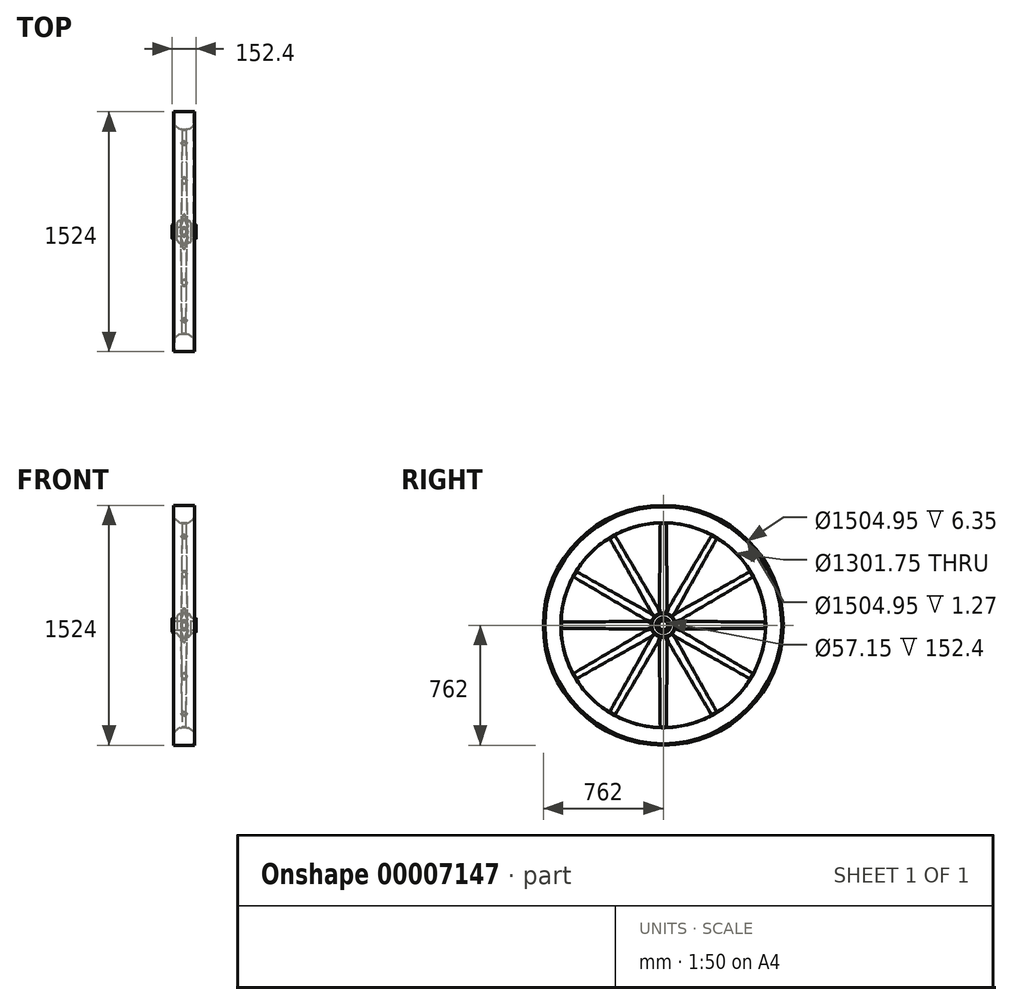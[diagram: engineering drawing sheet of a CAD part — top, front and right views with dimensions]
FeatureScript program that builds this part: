
annotation { "Feature Type Name" : "Feature", "Feature Type Description" : "" }
export const myFeature = defineFeature(function(context is Context, id is Id, definition is map)
    precondition{}
    {
        {
            var Q0;
            Q0=qCreatedBy(makeId("Front.planeOp"),FACE);
            var sketch = newSketch(context, id + "F0", { "sketchPlane" : qUnion([Q0])});
            skLineSegment(sketch, "E0", {"start": v(-76.2, 28.57) * mm, "end": v(76.2, 28.57) * mm});
            skLineSegment(sketch, "E1", {"start": v(76.2, 28.57) * mm, "end": v(76.2, 47.62) * mm});
            skLineSegment(sketch, "E2", {"start": v(76.2, 47.62) * mm, "end": v(44.45, 47.62) * mm});
            skLineSegment(sketch, "E3", {"start": v(44.45, 47.62) * mm, "end": v(44.45, 55.24) * mm});
            skLineSegment(sketch, "E4", {"start": v(44.45, 55.24) * mm, "end": v(31.75, 73.02) * mm});
            skLineSegment(sketch, "E5", {"start": v(31.75, 73.03) * mm, "end": v(-31.75, 73.03) * mm});
            skLineSegment(sketch, "E6", {"start": v(-31.75, 73.02) * mm, "end": v(-44.45, 55.24) * mm});
            skLineSegment(sketch, "E7", {"start": v(-44.45, 55.24) * mm, "end": v(-44.45, 47.62) * mm});
            skLineSegment(sketch, "E8", {"start": v(-44.45, 47.62) * mm, "end": v(-76.2, 47.62) * mm});
            skLineSegment(sketch, "E9", {"start": v(-76.2, 47.62) * mm, "end": v(-76.2, 28.58) * mm});
            skLineSegment(sketch, "E10", {"start": v(109.3, 0) * mm, "end": v(-114.89, 0) * mm, "construction": true});
            skLineSegment(sketch, "E11", {"start": v(-66.68, 762) * mm, "end": v(66.67, 762) * mm});
            skLineSegment(sketch, "E12", {"start": v(66.67, 762) * mm, "end": v(66.67, 752.48) * mm});
            skLineSegment(sketch, "E13", {"start": v(66.67, 752.48) * mm, "end": v(60.32, 752.48) * mm});
            skLineSegment(sketch, "E14", {"start": v(60.32, 752.48) * mm, "end": v(60.32, 676.28) * mm});
            skLineSegment(sketch, "E15", {"start": v(60.32, 676.28) * mm, "end": v(28.57, 650.88) * mm});
            skLineSegment(sketch, "E16", {"start": v(28.57, 650.88) * mm, "end": v(-28.58, 650.88) * mm});
            skLineSegment(sketch, "E17", {"start": v(-28.58, 650.88) * mm, "end": v(-60.33, 676.28) * mm});
            skLineSegment(sketch, "E18", {"start": v(-60.33, 676.28) * mm, "end": v(-60.33, 752.48) * mm});
            skLineSegment(sketch, "E19", {"start": v(-60.33, 752.48) * mm, "end": v(-66.68, 752.48) * mm});
            skLineSegment(sketch, "E20", {"start": v(-66.68, 752.48) * mm, "end": v(-66.68, 762) * mm});
            skSolve(sketch);
        }
        {
            var Q0;
            Q0=makeQuery(id+"F0.imprint","IMPRINT",FACE,{"disambiguationData":[TD([[makeQuery(id+"F0.imprint","IMPRINT",EDGE,{"derivedFrom":sQuery(id+"F0.wireOp",EDGE,"E11")}),-1.0]])]});
            var Q1;
            Q1=makeQuery(id+"F0.imprint","IMPRINT",FACE,{"disambiguationData":[TD([[makeQuery(id+"F0.imprint","IMPRINT",EDGE,{"derivedFrom":sQuery(id+"F0.wireOp",EDGE,"E0")}),1.0]])]});
            var Q2;
            Q2=sQuery(id+"F0.wireOp",EDGE,"E10");
            revolve(context, id + "F1", {"entities" : qUnion([Q0, Q1]), "axis" : qUnion([Q2]), "revolveType" : RevolveType.FULL});
        }
        {
            var Q0;
            Q0=makeQuery(id+"F1.opRevolve","SWEPT_EDGE",EDGE,{"disambiguationData":[OSD([sQuery(id+"F0.wireOp",EDGE,"E7"),sQuery(id+"F0.wireOp",EDGE,"E8")])]});
            var Q1;
            Q1=makeQuery(id+"F1.opRevolve","SWEPT_EDGE",EDGE,{"disambiguationData":[OSD([sQuery(id+"F0.wireOp",EDGE,"E6"),sQuery(id+"F0.wireOp",EDGE,"E7")])]});
            var Q2;
            Q2=makeQuery(id+"F1.opRevolve","SWEPT_EDGE",EDGE,{"disambiguationData":[OSD([sQuery(id+"F0.wireOp",EDGE,"E5"),sQuery(id+"F0.wireOp",EDGE,"E6")])]});
            var Q3;
            Q3=makeQuery(id+"F1.opRevolve","SWEPT_EDGE",EDGE,{"disambiguationData":[OSD([sQuery(id+"F0.wireOp",EDGE,"E4"),sQuery(id+"F0.wireOp",EDGE,"E5")])]});
            var Q4;
            Q4=makeQuery(id+"F1.opRevolve","SWEPT_EDGE",EDGE,{"disambiguationData":[OSD([sQuery(id+"F0.wireOp",EDGE,"E3"),sQuery(id+"F0.wireOp",EDGE,"E4")])]});
            var Q5;
            Q5=makeQuery(id+"F1.opRevolve","SWEPT_EDGE",EDGE,{"disambiguationData":[OSD([sQuery(id+"F0.wireOp",EDGE,"E2"),sQuery(id+"F0.wireOp",EDGE,"E3")])]});
            fillet(context, id + "F2", {"entities" : qUnion([Q0, Q1, Q2, Q3, Q4, Q5]), "radius" : 5.08 * mm, "tangentPropagation" : true, "allowEdgeOverflow" : false});
        }
        {
            var Q0;
            Q0=makeQuery(id+"F1.opRevolve","SWEPT_EDGE",EDGE,{"disambiguationData":[OSD([sQuery(id+"F0.wireOp",EDGE,"E1"),sQuery(id+"F0.wireOp",EDGE,"E2")])]});
            var Q1;
            Q1=makeQuery(id+"F1.opRevolve","SWEPT_EDGE",EDGE,{"disambiguationData":[OSD([sQuery(id+"F0.wireOp",EDGE,"E8"),sQuery(id+"F0.wireOp",EDGE,"E9")])]});
            fillet(context, id + "F3", {"entities" : qUnion([Q0, Q1]), "radius" : 7.62 * mm, "tangentPropagation" : true, "allowEdgeOverflow" : false});
        }
        {
            var Q0;
            Q0=makeQuery(id+"F1.opRevolve","SWEPT_EDGE",EDGE,{"disambiguationData":[OSD([sQuery(id+"F0.wireOp",EDGE,"E17"),sQuery(id+"F0.wireOp",EDGE,"E18")])]});
            var Q1;
            Q1=makeQuery(id+"F1.opRevolve","SWEPT_EDGE",EDGE,{"disambiguationData":[OSD([sQuery(id+"F0.wireOp",EDGE,"E16"),sQuery(id+"F0.wireOp",EDGE,"E17")])]});
            var Q2;
            Q2=makeQuery(id+"F1.opRevolve","SWEPT_EDGE",EDGE,{"disambiguationData":[OSD([sQuery(id+"F0.wireOp",EDGE,"E15"),sQuery(id+"F0.wireOp",EDGE,"E16")])]});
            var Q3;
            Q3=makeQuery(id+"F1.opRevolve","SWEPT_EDGE",EDGE,{"disambiguationData":[OSD([sQuery(id+"F0.wireOp",EDGE,"E14"),sQuery(id+"F0.wireOp",EDGE,"E15")])]});
            fillet(context, id + "F4", {"entities" : qUnion([Q0, Q1, Q2, Q3]), "radius" : 12.7 * mm, "tangentPropagation" : true, "allowEdgeOverflow" : false});
        }
        {
            var Q0;
            Q0=makeQuery(id+"F1.opRevolve","SWEPT_EDGE",EDGE,{"disambiguationData":[OSD([sQuery(id+"F0.wireOp",EDGE,"E13"),sQuery(id+"F0.wireOp",EDGE,"E14")])]});
            fillet(context, id + "F5", {"entities" : qUnion([Q0]), "radius" : 5.08 * mm, "tangentPropagation" : true, "allowEdgeOverflow" : false});
        }
        {
            var Q0;
            Q0=qCreatedBy(makeId("Front.planeOp"),FACE);
            cPlane(context, id + "F6", {"entities" : qUnion([Q0]), "cplaneType" : CPlaneType.OFFSET, "offset" : 50.8 * mm, "oppositeDirection" : true, "width" : 152.4 * mm, "height" : 152.4 * mm});
        }
        {
            var Q0;
            Q0=qCreatedBy(makeId("Front.planeOp"),FACE);
            cPlane(context, id + "F7", {"entities" : qUnion([Q0]), "cplaneType" : CPlaneType.OFFSET, "offset" : 654.05 * mm, "oppositeDirection" : true, "width" : 152.4 * mm, "height" : 152.4 * mm});
        }
        {
            var Q0;
            Q0=qCreatedBy(id+"F6.planeOp",FACE);
            var sketch = newSketch(context, id + "F8", { "sketchPlane" : qUnion([Q0])});
            skEllipse(sketch, "E21", {"center": v(0, 0) * mm, "majorRadius": 25.4 * mm, "minorRadius": 19.05 * mm, "majorAxis": v(0, 1)});
            skSolve(sketch);
        }
        {
            var Q0;
            Q0=qCreatedBy(id+"F7.planeOp",FACE);
            var sketch = newSketch(context, id + "F9", { "sketchPlane" : qUnion([Q0])});
            skEllipse(sketch, "E22", {"center": v(0, 0) * mm, "majorRadius": 19.05 * mm, "minorRadius": 12.7 * mm, "majorAxis": v(0, 1)});
            skSolve(sketch);
        }
        {
            var Q0;
            Q0=makeQuery(id+"F8.imprint","IMPRINT",FACE,{"disambiguationData":[TD([[makeQuery(id+"F8.imprint","IMPRINT",EDGE,{"derivedFrom":sQuery(id+"F8.wireOp",EDGE,"E21")}),1.0]])]});
            var Q1;
            Q1=makeQuery(id+"F9.imprint","IMPRINT",FACE,{"disambiguationData":[TD([[makeQuery(id+"F9.imprint","IMPRINT",EDGE,{"derivedFrom":sQuery(id+"F9.wireOp",EDGE,"E22")}),1.0]])]});
            loft(context, id + "F10", {"sheetProfilesArray" : [{ "sheetProfileEntities" : qUnion([Q0]) }, { "sheetProfileEntities" : qUnion([Q1]) }]});
        }
        {
            var Q0;
            Q0=makeQuery(id+"F10.opLoft","SWEPT_BODY",BODY,{"disambiguationData":[OSD([makeQuery(id+"F8.imprint","IMPRINT",FACE,{"disambiguationData":[TD([[makeQuery(id+"F8.imprint","IMPRINT",EDGE,{"derivedFrom":sQuery(id+"F8.wireOp",EDGE,"E21")}),1.0]])]}),makeQuery(id+"F9.imprint","IMPRINT",FACE,{"disambiguationData":[TD([[makeQuery(id+"F9.imprint","IMPRINT",EDGE,{"derivedFrom":sQuery(id+"F9.wireOp",EDGE,"E22")}),1.0]])]})])]});
            var Q1;
            Q1=makeQuery(id+"F1.opRevolve","SWEPT_EDGE",EDGE,{"disambiguationData":[OSD([sQuery(id+"F0.wireOp",EDGE,"E0"),sQuery(id+"F0.wireOp",EDGE,"E1")])]});
            circularPattern(context, id + "F11", {"entities" : qUnion([Q0]), "axis" : qUnion([Q1]), "angle" : 30 * degree, "instanceCount" : 12});
        }
        {
            var Q0;
            Q0=makeQuery(id+"F10.opLoft","SWEPT_BODY",BODY,{"disambiguationData":[OSD([makeQuery(id+"F8.imprint","IMPRINT",FACE,{"disambiguationData":[TD([[makeQuery(id+"F8.imprint","IMPRINT",EDGE,{"derivedFrom":sQuery(id+"F8.wireOp",EDGE,"E21")}),1.0]])]}),makeQuery(id+"F9.imprint","IMPRINT",FACE,{"disambiguationData":[TD([[makeQuery(id+"F9.imprint","IMPRINT",EDGE,{"derivedFrom":sQuery(id+"F9.wireOp",EDGE,"E22")}),1.0]])]})])]});
            var Q1;
            Q1=makeQuery(id+"F1.opRevolve","SWEPT_BODY",BODY,{"disambiguationData":[OSD([sQuery(id+"F0.wireOp",EDGE,"E0"),sQuery(id+"F0.wireOp",EDGE,"E1"),sQuery(id+"F0.wireOp",EDGE,"E2"),sQuery(id+"F0.wireOp",EDGE,"E3"),sQuery(id+"F0.wireOp",EDGE,"E4"),sQuery(id+"F0.wireOp",EDGE,"E5"),sQuery(id+"F0.wireOp",EDGE,"E6"),sQuery(id+"F0.wireOp",EDGE,"E7"),sQuery(id+"F0.wireOp",EDGE,"E8"),sQuery(id+"F0.wireOp",EDGE,"E9")])]});
            var Q2;
            Q2=makeQuery(id+"F11.opPattern","COPY",BODY,{"derivedFrom":makeQuery(id+"F10.opLoft","SWEPT_BODY",BODY,{"disambiguationData":[OSD([makeQuery(id+"F8.imprint","IMPRINT",FACE,{"disambiguationData":[TD([[makeQuery(id+"F8.imprint","IMPRINT",EDGE,{"derivedFrom":sQuery(id+"F8.wireOp",EDGE,"E21")}),1.0]])]}),makeQuery(id+"F9.imprint","IMPRINT",FACE,{"disambiguationData":[TD([[makeQuery(id+"F9.imprint","IMPRINT",EDGE,{"derivedFrom":sQuery(id+"F9.wireOp",EDGE,"E22")}),1.0]])]})])]}),"instanceName":"1"});
            var Q3;
            Q3=makeQuery(id+"F11.opPattern","COPY",BODY,{"derivedFrom":makeQuery(id+"F10.opLoft","SWEPT_BODY",BODY,{"disambiguationData":[OSD([makeQuery(id+"F8.imprint","IMPRINT",FACE,{"disambiguationData":[TD([[makeQuery(id+"F8.imprint","IMPRINT",EDGE,{"derivedFrom":sQuery(id+"F8.wireOp",EDGE,"E21")}),1.0]])]}),makeQuery(id+"F9.imprint","IMPRINT",FACE,{"disambiguationData":[TD([[makeQuery(id+"F9.imprint","IMPRINT",EDGE,{"derivedFrom":sQuery(id+"F9.wireOp",EDGE,"E22")}),1.0]])]})])]}),"instanceName":"2"});
            var Q4;
            Q4=makeQuery(id+"F11.opPattern","COPY",BODY,{"derivedFrom":makeQuery(id+"F10.opLoft","SWEPT_BODY",BODY,{"disambiguationData":[OSD([makeQuery(id+"F8.imprint","IMPRINT",FACE,{"disambiguationData":[TD([[makeQuery(id+"F8.imprint","IMPRINT",EDGE,{"derivedFrom":sQuery(id+"F8.wireOp",EDGE,"E21")}),1.0]])]}),makeQuery(id+"F9.imprint","IMPRINT",FACE,{"disambiguationData":[TD([[makeQuery(id+"F9.imprint","IMPRINT",EDGE,{"derivedFrom":sQuery(id+"F9.wireOp",EDGE,"E22")}),1.0]])]})])]}),"instanceName":"3"});
            var Q5;
            Q5=makeQuery(id+"F11.opPattern","COPY",BODY,{"derivedFrom":makeQuery(id+"F10.opLoft","SWEPT_BODY",BODY,{"disambiguationData":[OSD([makeQuery(id+"F8.imprint","IMPRINT",FACE,{"disambiguationData":[TD([[makeQuery(id+"F8.imprint","IMPRINT",EDGE,{"derivedFrom":sQuery(id+"F8.wireOp",EDGE,"E21")}),1.0]])]}),makeQuery(id+"F9.imprint","IMPRINT",FACE,{"disambiguationData":[TD([[makeQuery(id+"F9.imprint","IMPRINT",EDGE,{"derivedFrom":sQuery(id+"F9.wireOp",EDGE,"E22")}),1.0]])]})])]}),"instanceName":"4"});
            var Q6;
            Q6=makeQuery(id+"F11.opPattern","COPY",BODY,{"derivedFrom":makeQuery(id+"F10.opLoft","SWEPT_BODY",BODY,{"disambiguationData":[OSD([makeQuery(id+"F8.imprint","IMPRINT",FACE,{"disambiguationData":[TD([[makeQuery(id+"F8.imprint","IMPRINT",EDGE,{"derivedFrom":sQuery(id+"F8.wireOp",EDGE,"E21")}),1.0]])]}),makeQuery(id+"F9.imprint","IMPRINT",FACE,{"disambiguationData":[TD([[makeQuery(id+"F9.imprint","IMPRINT",EDGE,{"derivedFrom":sQuery(id+"F9.wireOp",EDGE,"E22")}),1.0]])]})])]}),"instanceName":"5"});
            var Q7;
            Q7=makeQuery(id+"F11.opPattern","COPY",BODY,{"derivedFrom":makeQuery(id+"F10.opLoft","SWEPT_BODY",BODY,{"disambiguationData":[OSD([makeQuery(id+"F8.imprint","IMPRINT",FACE,{"disambiguationData":[TD([[makeQuery(id+"F8.imprint","IMPRINT",EDGE,{"derivedFrom":sQuery(id+"F8.wireOp",EDGE,"E21")}),1.0]])]}),makeQuery(id+"F9.imprint","IMPRINT",FACE,{"disambiguationData":[TD([[makeQuery(id+"F9.imprint","IMPRINT",EDGE,{"derivedFrom":sQuery(id+"F9.wireOp",EDGE,"E22")}),1.0]])]})])]}),"instanceName":"6"});
            var Q8;
            Q8=makeQuery(id+"F11.opPattern","COPY",BODY,{"derivedFrom":makeQuery(id+"F10.opLoft","SWEPT_BODY",BODY,{"disambiguationData":[OSD([makeQuery(id+"F8.imprint","IMPRINT",FACE,{"disambiguationData":[TD([[makeQuery(id+"F8.imprint","IMPRINT",EDGE,{"derivedFrom":sQuery(id+"F8.wireOp",EDGE,"E21")}),1.0]])]}),makeQuery(id+"F9.imprint","IMPRINT",FACE,{"disambiguationData":[TD([[makeQuery(id+"F9.imprint","IMPRINT",EDGE,{"derivedFrom":sQuery(id+"F9.wireOp",EDGE,"E22")}),1.0]])]})])]}),"instanceName":"7"});
            var Q9;
            Q9=makeQuery(id+"F11.opPattern","COPY",BODY,{"derivedFrom":makeQuery(id+"F10.opLoft","SWEPT_BODY",BODY,{"disambiguationData":[OSD([makeQuery(id+"F8.imprint","IMPRINT",FACE,{"disambiguationData":[TD([[makeQuery(id+"F8.imprint","IMPRINT",EDGE,{"derivedFrom":sQuery(id+"F8.wireOp",EDGE,"E21")}),1.0]])]}),makeQuery(id+"F9.imprint","IMPRINT",FACE,{"disambiguationData":[TD([[makeQuery(id+"F9.imprint","IMPRINT",EDGE,{"derivedFrom":sQuery(id+"F9.wireOp",EDGE,"E22")}),1.0]])]})])]}),"instanceName":"8"});
            var Q10;
            Q10=makeQuery(id+"F11.opPattern","COPY",BODY,{"derivedFrom":makeQuery(id+"F10.opLoft","SWEPT_BODY",BODY,{"disambiguationData":[OSD([makeQuery(id+"F8.imprint","IMPRINT",FACE,{"disambiguationData":[TD([[makeQuery(id+"F8.imprint","IMPRINT",EDGE,{"derivedFrom":sQuery(id+"F8.wireOp",EDGE,"E21")}),1.0]])]}),makeQuery(id+"F9.imprint","IMPRINT",FACE,{"disambiguationData":[TD([[makeQuery(id+"F9.imprint","IMPRINT",EDGE,{"derivedFrom":sQuery(id+"F9.wireOp",EDGE,"E22")}),1.0]])]})])]}),"instanceName":"9"});
            var Q11;
            Q11=makeQuery(id+"F11.opPattern","COPY",BODY,{"derivedFrom":makeQuery(id+"F10.opLoft","SWEPT_BODY",BODY,{"disambiguationData":[OSD([makeQuery(id+"F8.imprint","IMPRINT",FACE,{"disambiguationData":[TD([[makeQuery(id+"F8.imprint","IMPRINT",EDGE,{"derivedFrom":sQuery(id+"F8.wireOp",EDGE,"E21")}),1.0]])]}),makeQuery(id+"F9.imprint","IMPRINT",FACE,{"disambiguationData":[TD([[makeQuery(id+"F9.imprint","IMPRINT",EDGE,{"derivedFrom":sQuery(id+"F9.wireOp",EDGE,"E22")}),1.0]])]})])]}),"instanceName":"10"});
            var Q12;
            Q12=makeQuery(id+"F11.opPattern","COPY",BODY,{"derivedFrom":makeQuery(id+"F10.opLoft","SWEPT_BODY",BODY,{"disambiguationData":[OSD([makeQuery(id+"F8.imprint","IMPRINT",FACE,{"disambiguationData":[TD([[makeQuery(id+"F8.imprint","IMPRINT",EDGE,{"derivedFrom":sQuery(id+"F8.wireOp",EDGE,"E21")}),1.0]])]}),makeQuery(id+"F9.imprint","IMPRINT",FACE,{"disambiguationData":[TD([[makeQuery(id+"F9.imprint","IMPRINT",EDGE,{"derivedFrom":sQuery(id+"F9.wireOp",EDGE,"E22")}),1.0]])]})])]}),"instanceName":"11"});
            booleanBodies(context, id + "F12", {"operationType" : BooleanOperationType.UNION, "tools" : qUnion([Q0, Q1, Q2, Q3, Q4, Q5, Q6, Q7, Q8, Q9, Q10, Q11, Q12])});
        }
        {
            var Q0;
            {var subQ0=makeQuery(id+"F10.opLoft","SWEPT_FACE",FACE,{"disambiguationData":[OSD([sQuery(id+"F8.wireOp",EDGE,"E21"),sQuery(id+"F9.wireOp",EDGE,"E22")])]});Q0=makeQuery(id+"F12.opBoolean","INTERSECT",EDGE,{"derivedFrom":[subQ0,makeQuery(id+"F11.opPattern","COPY",FACE,{"derivedFrom":subQ0,"instanceName":"11"})]});}
            var Q1;
            Q1=makeQuery(id+"F12.opBoolean","INTERSECT",EDGE,{"disambiguationData":[OD(0.0)],"derivedFrom":[makeQuery(id+"F1.opRevolve","SWEPT_FACE",FACE,{"disambiguationData":[OSD([sQuery(id+"F0.wireOp",EDGE,"E5")])]}),makeQuery(id+"F10.opLoft","SWEPT_FACE",FACE,{"disambiguationData":[OSD([sQuery(id+"F8.wireOp",EDGE,"E21"),sQuery(id+"F9.wireOp",EDGE,"E22")])]})]});
            var Q2;
            Q2=makeQuery(id+"F12.opBoolean","INTERSECT",EDGE,{"disambiguationData":[OD(0.0)],"derivedFrom":[makeQuery(id+"F1.opRevolve","SWEPT_FACE",FACE,{"disambiguationData":[OSD([sQuery(id+"F0.wireOp",EDGE,"E5")])]}),makeQuery(id+"F11.opPattern","COPY",FACE,{"derivedFrom":makeQuery(id+"F10.opLoft","SWEPT_FACE",FACE,{"disambiguationData":[OSD([sQuery(id+"F8.wireOp",EDGE,"E21"),sQuery(id+"F9.wireOp",EDGE,"E22")])]}),"instanceName":"11"})]});
            var Q3;
            Q3=makeQuery(id+"F12.opBoolean","INTERSECT",EDGE,{"disambiguationData":[OD(0.0)],"derivedFrom":[makeQuery(id+"F1.opRevolve","SWEPT_FACE",FACE,{"disambiguationData":[OSD([sQuery(id+"F0.wireOp",EDGE,"E5")])]}),makeQuery(id+"F11.opPattern","COPY",FACE,{"derivedFrom":makeQuery(id+"F10.opLoft","SWEPT_FACE",FACE,{"disambiguationData":[OSD([sQuery(id+"F8.wireOp",EDGE,"E21"),sQuery(id+"F9.wireOp",EDGE,"E22")])]}),"instanceName":"10"})]});
            var Q4;
            {var subQ0=makeQuery(id+"F10.opLoft","SWEPT_FACE",FACE,{"disambiguationData":[OSD([sQuery(id+"F8.wireOp",EDGE,"E21"),sQuery(id+"F9.wireOp",EDGE,"E22")])]});Q4=makeQuery(id+"F12.opBoolean","INTERSECT",EDGE,{"derivedFrom":[makeQuery(id+"F11.opPattern","COPY",FACE,{"derivedFrom":subQ0,"instanceName":"10"}),makeQuery(id+"F11.opPattern","COPY",FACE,{"derivedFrom":subQ0,"instanceName":"11"})]});}
            var Q5;
            {var subQ0=makeQuery(id+"F10.opLoft","SWEPT_FACE",FACE,{"disambiguationData":[OSD([sQuery(id+"F8.wireOp",EDGE,"E21"),sQuery(id+"F9.wireOp",EDGE,"E22")])]});Q5=makeQuery(id+"F12.opBoolean","INTERSECT",EDGE,{"derivedFrom":[makeQuery(id+"F11.opPattern","COPY",FACE,{"derivedFrom":subQ0,"instanceName":"9"}),makeQuery(id+"F11.opPattern","COPY",FACE,{"derivedFrom":subQ0,"instanceName":"10"})]});}
            var Q6;
            Q6=makeQuery(id+"F12.opBoolean","INTERSECT",EDGE,{"disambiguationData":[OD(0.0)],"derivedFrom":[makeQuery(id+"F1.opRevolve","SWEPT_FACE",FACE,{"disambiguationData":[OSD([sQuery(id+"F0.wireOp",EDGE,"E5")])]}),makeQuery(id+"F11.opPattern","COPY",FACE,{"derivedFrom":makeQuery(id+"F10.opLoft","SWEPT_FACE",FACE,{"disambiguationData":[OSD([sQuery(id+"F8.wireOp",EDGE,"E21"),sQuery(id+"F9.wireOp",EDGE,"E22")])]}),"instanceName":"9"})]});
            var Q7;
            {var subQ0=makeQuery(id+"F10.opLoft","SWEPT_FACE",FACE,{"disambiguationData":[OSD([sQuery(id+"F8.wireOp",EDGE,"E21"),sQuery(id+"F9.wireOp",EDGE,"E22")])]});Q7=makeQuery(id+"F12.opBoolean","INTERSECT",EDGE,{"derivedFrom":[makeQuery(id+"F11.opPattern","COPY",FACE,{"derivedFrom":subQ0,"instanceName":"8"}),makeQuery(id+"F11.opPattern","COPY",FACE,{"derivedFrom":subQ0,"instanceName":"9"})]});}
            var Q8;
            Q8=makeQuery(id+"F12.opBoolean","INTERSECT",EDGE,{"disambiguationData":[OD(0.0)],"derivedFrom":[makeQuery(id+"F1.opRevolve","SWEPT_FACE",FACE,{"disambiguationData":[OSD([sQuery(id+"F0.wireOp",EDGE,"E5")])]}),makeQuery(id+"F11.opPattern","COPY",FACE,{"derivedFrom":makeQuery(id+"F10.opLoft","SWEPT_FACE",FACE,{"disambiguationData":[OSD([sQuery(id+"F8.wireOp",EDGE,"E21"),sQuery(id+"F9.wireOp",EDGE,"E22")])]}),"instanceName":"8"})]});
            var Q9;
            {var subQ0=makeQuery(id+"F10.opLoft","SWEPT_FACE",FACE,{"disambiguationData":[OSD([sQuery(id+"F8.wireOp",EDGE,"E21"),sQuery(id+"F9.wireOp",EDGE,"E22")])]});Q9=makeQuery(id+"F12.opBoolean","INTERSECT",EDGE,{"derivedFrom":[makeQuery(id+"F11.opPattern","COPY",FACE,{"derivedFrom":subQ0,"instanceName":"7"}),makeQuery(id+"F11.opPattern","COPY",FACE,{"derivedFrom":subQ0,"instanceName":"8"})]});}
            var Q10;
            Q10=makeQuery(id+"F12.opBoolean","INTERSECT",EDGE,{"disambiguationData":[OD(0.0)],"derivedFrom":[makeQuery(id+"F1.opRevolve","SWEPT_FACE",FACE,{"disambiguationData":[OSD([sQuery(id+"F0.wireOp",EDGE,"E5")])]}),makeQuery(id+"F11.opPattern","COPY",FACE,{"derivedFrom":makeQuery(id+"F10.opLoft","SWEPT_FACE",FACE,{"disambiguationData":[OSD([sQuery(id+"F8.wireOp",EDGE,"E21"),sQuery(id+"F9.wireOp",EDGE,"E22")])]}),"instanceName":"7"})]});
            var Q11;
            {var subQ0=makeQuery(id+"F10.opLoft","SWEPT_FACE",FACE,{"disambiguationData":[OSD([sQuery(id+"F8.wireOp",EDGE,"E21"),sQuery(id+"F9.wireOp",EDGE,"E22")])]});Q11=makeQuery(id+"F12.opBoolean","INTERSECT",EDGE,{"derivedFrom":[makeQuery(id+"F11.opPattern","COPY",FACE,{"derivedFrom":subQ0,"instanceName":"6"}),makeQuery(id+"F11.opPattern","COPY",FACE,{"derivedFrom":subQ0,"instanceName":"7"})]});}
            var Q12;
            Q12=makeQuery(id+"F12.opBoolean","INTERSECT",EDGE,{"disambiguationData":[OD(0.0)],"derivedFrom":[makeQuery(id+"F1.opRevolve","SWEPT_FACE",FACE,{"disambiguationData":[OSD([sQuery(id+"F0.wireOp",EDGE,"E5")])]}),makeQuery(id+"F11.opPattern","COPY",FACE,{"derivedFrom":makeQuery(id+"F10.opLoft","SWEPT_FACE",FACE,{"disambiguationData":[OSD([sQuery(id+"F8.wireOp",EDGE,"E21"),sQuery(id+"F9.wireOp",EDGE,"E22")])]}),"instanceName":"6"})]});
            var Q13;
            {var subQ0=makeQuery(id+"F10.opLoft","SWEPT_FACE",FACE,{"disambiguationData":[OSD([sQuery(id+"F8.wireOp",EDGE,"E21"),sQuery(id+"F9.wireOp",EDGE,"E22")])]});Q13=makeQuery(id+"F12.opBoolean","INTERSECT",EDGE,{"derivedFrom":[makeQuery(id+"F11.opPattern","COPY",FACE,{"derivedFrom":subQ0,"instanceName":"5"}),makeQuery(id+"F11.opPattern","COPY",FACE,{"derivedFrom":subQ0,"instanceName":"6"})]});}
            var Q14;
            Q14=makeQuery(id+"F12.opBoolean","INTERSECT",EDGE,{"disambiguationData":[OD(0.0)],"derivedFrom":[makeQuery(id+"F1.opRevolve","SWEPT_FACE",FACE,{"disambiguationData":[OSD([sQuery(id+"F0.wireOp",EDGE,"E5")])]}),makeQuery(id+"F11.opPattern","COPY",FACE,{"derivedFrom":makeQuery(id+"F10.opLoft","SWEPT_FACE",FACE,{"disambiguationData":[OSD([sQuery(id+"F8.wireOp",EDGE,"E21"),sQuery(id+"F9.wireOp",EDGE,"E22")])]}),"instanceName":"5"})]});
            var Q15;
            {var subQ0=makeQuery(id+"F10.opLoft","SWEPT_FACE",FACE,{"disambiguationData":[OSD([sQuery(id+"F8.wireOp",EDGE,"E21"),sQuery(id+"F9.wireOp",EDGE,"E22")])]});Q15=makeQuery(id+"F12.opBoolean","INTERSECT",EDGE,{"derivedFrom":[makeQuery(id+"F11.opPattern","COPY",FACE,{"derivedFrom":subQ0,"instanceName":"4"}),makeQuery(id+"F11.opPattern","COPY",FACE,{"derivedFrom":subQ0,"instanceName":"5"})]});}
            var Q16;
            Q16=makeQuery(id+"F12.opBoolean","INTERSECT",EDGE,{"disambiguationData":[OD(0.0)],"derivedFrom":[makeQuery(id+"F1.opRevolve","SWEPT_FACE",FACE,{"disambiguationData":[OSD([sQuery(id+"F0.wireOp",EDGE,"E5")])]}),makeQuery(id+"F11.opPattern","COPY",FACE,{"derivedFrom":makeQuery(id+"F10.opLoft","SWEPT_FACE",FACE,{"disambiguationData":[OSD([sQuery(id+"F8.wireOp",EDGE,"E21"),sQuery(id+"F9.wireOp",EDGE,"E22")])]}),"instanceName":"4"})]});
            var Q17;
            {var subQ0=makeQuery(id+"F10.opLoft","SWEPT_FACE",FACE,{"disambiguationData":[OSD([sQuery(id+"F8.wireOp",EDGE,"E21"),sQuery(id+"F9.wireOp",EDGE,"E22")])]});Q17=makeQuery(id+"F12.opBoolean","INTERSECT",EDGE,{"derivedFrom":[makeQuery(id+"F11.opPattern","COPY",FACE,{"derivedFrom":subQ0,"instanceName":"3"}),makeQuery(id+"F11.opPattern","COPY",FACE,{"derivedFrom":subQ0,"instanceName":"4"})]});}
            var Q18;
            Q18=makeQuery(id+"F12.opBoolean","INTERSECT",EDGE,{"disambiguationData":[OD(0.0)],"derivedFrom":[makeQuery(id+"F1.opRevolve","SWEPT_FACE",FACE,{"disambiguationData":[OSD([sQuery(id+"F0.wireOp",EDGE,"E5")])]}),makeQuery(id+"F11.opPattern","COPY",FACE,{"derivedFrom":makeQuery(id+"F10.opLoft","SWEPT_FACE",FACE,{"disambiguationData":[OSD([sQuery(id+"F8.wireOp",EDGE,"E21"),sQuery(id+"F9.wireOp",EDGE,"E22")])]}),"instanceName":"3"})]});
            var Q19;
            Q19=makeQuery(id+"F12.opBoolean","INTERSECT",EDGE,{"disambiguationData":[OD(0.0)],"derivedFrom":[makeQuery(id+"F1.opRevolve","SWEPT_FACE",FACE,{"disambiguationData":[OSD([sQuery(id+"F0.wireOp",EDGE,"E5")])]}),makeQuery(id+"F11.opPattern","COPY",FACE,{"derivedFrom":makeQuery(id+"F10.opLoft","SWEPT_FACE",FACE,{"disambiguationData":[OSD([sQuery(id+"F8.wireOp",EDGE,"E21"),sQuery(id+"F9.wireOp",EDGE,"E22")])]}),"instanceName":"2"})]});
            var Q20;
            {var subQ0=makeQuery(id+"F10.opLoft","SWEPT_FACE",FACE,{"disambiguationData":[OSD([sQuery(id+"F8.wireOp",EDGE,"E21"),sQuery(id+"F9.wireOp",EDGE,"E22")])]});Q20=makeQuery(id+"F12.opBoolean","INTERSECT",EDGE,{"derivedFrom":[makeQuery(id+"F11.opPattern","COPY",FACE,{"derivedFrom":subQ0,"instanceName":"2"}),makeQuery(id+"F11.opPattern","COPY",FACE,{"derivedFrom":subQ0,"instanceName":"3"})]});}
            var Q21;
            Q21=makeQuery(id+"F12.opBoolean","INTERSECT",EDGE,{"disambiguationData":[OD(0.0)],"derivedFrom":[makeQuery(id+"F1.opRevolve","SWEPT_FACE",FACE,{"disambiguationData":[OSD([sQuery(id+"F0.wireOp",EDGE,"E5")])]}),makeQuery(id+"F11.opPattern","COPY",FACE,{"derivedFrom":makeQuery(id+"F10.opLoft","SWEPT_FACE",FACE,{"disambiguationData":[OSD([sQuery(id+"F8.wireOp",EDGE,"E21"),sQuery(id+"F9.wireOp",EDGE,"E22")])]}),"instanceName":"1"})]});
            var Q22;
            {var subQ0=makeQuery(id+"F10.opLoft","SWEPT_FACE",FACE,{"disambiguationData":[OSD([sQuery(id+"F8.wireOp",EDGE,"E21"),sQuery(id+"F9.wireOp",EDGE,"E22")])]});Q22=makeQuery(id+"F12.opBoolean","INTERSECT",EDGE,{"derivedFrom":[makeQuery(id+"F11.opPattern","COPY",FACE,{"derivedFrom":subQ0,"instanceName":"1"}),makeQuery(id+"F11.opPattern","COPY",FACE,{"derivedFrom":subQ0,"instanceName":"2"})]});}
            var Q23;
            {var subQ0=makeQuery(id+"F10.opLoft","SWEPT_FACE",FACE,{"disambiguationData":[OSD([sQuery(id+"F8.wireOp",EDGE,"E21"),sQuery(id+"F9.wireOp",EDGE,"E22")])]});Q23=makeQuery(id+"F12.opBoolean","INTERSECT",EDGE,{"derivedFrom":[subQ0,makeQuery(id+"F11.opPattern","COPY",FACE,{"derivedFrom":subQ0,"instanceName":"1"})]});}
            fillet(context, id + "F13", {"entities" : qUnion([Q0, Q1, Q2, Q3, Q4, Q5, Q6, Q7, Q8, Q9, Q10, Q11, Q12, Q13, Q14, Q15, Q16, Q17, Q18, Q19, Q20, Q21, Q22, Q23]), "radius" : 5.08 * mm, "tangentPropagation" : true, "allowEdgeOverflow" : false});
        }
        {
            var Q0;
            Q0=makeQuery(id+"F12.opBoolean","INTERSECT",EDGE,{"disambiguationData":[OD(1.0)],"derivedFrom":[makeQuery(id+"F1.opRevolve","SWEPT_FACE",FACE,{"disambiguationData":[OSD([sQuery(id+"F0.wireOp",EDGE,"E5")])]}),makeQuery(id+"F11.opPattern","COPY",FACE,{"derivedFrom":makeQuery(id+"F10.opLoft","SWEPT_FACE",FACE,{"disambiguationData":[OSD([sQuery(id+"F8.wireOp",EDGE,"E21"),sQuery(id+"F9.wireOp",EDGE,"E22")])]}),"instanceName":"3"})]});
            fillet(context, id + "F14", {"entities" : qUnion([Q0]), "radius" : 5.08 * mm, "tangentPropagation" : true, "allowEdgeOverflow" : false});
        }
        {
            var Q0;
            Q0=makeQuery(id+"F1.opRevolve","SWEPT_BODY",BODY,{"disambiguationData":[OSD([sQuery(id+"F0.wireOp",EDGE,"E11"),sQuery(id+"F0.wireOp",EDGE,"E12"),sQuery(id+"F0.wireOp",EDGE,"E13"),sQuery(id+"F0.wireOp",EDGE,"E14"),sQuery(id+"F0.wireOp",EDGE,"E15"),sQuery(id+"F0.wireOp",EDGE,"E16"),sQuery(id+"F0.wireOp",EDGE,"E17"),sQuery(id+"F0.wireOp",EDGE,"E18"),sQuery(id+"F0.wireOp",EDGE,"E19"),sQuery(id+"F0.wireOp",EDGE,"E20")])]});
            var Q1;
            Q1=makeQuery(id+"F10.opLoft","SWEPT_BODY",BODY,{"disambiguationData":[OSD([makeQuery(id+"F8.imprint","IMPRINT",FACE,{"disambiguationData":[TD([[makeQuery(id+"F8.imprint","IMPRINT",EDGE,{"derivedFrom":sQuery(id+"F8.wireOp",EDGE,"E21")}),1.0]])]}),makeQuery(id+"F9.imprint","IMPRINT",FACE,{"disambiguationData":[TD([[makeQuery(id+"F9.imprint","IMPRINT",EDGE,{"derivedFrom":sQuery(id+"F9.wireOp",EDGE,"E22")}),1.0]])]})])]});
            booleanBodies(context, id + "F15", {"operationType" : BooleanOperationType.UNION, "tools" : qUnion([Q0, Q1])});
        }
        {
            var Q0;
            Q0=makeQuery(id+"F15.opBoolean","INTERSECT",EDGE,{"derivedFrom":[makeQuery(id+"F1.opRevolve","SWEPT_FACE",FACE,{"disambiguationData":[OSD([sQuery(id+"F0.wireOp",EDGE,"E16")])]}),makeQuery(id+"F11.opPattern","COPY",FACE,{"derivedFrom":makeQuery(id+"F10.opLoft","SWEPT_FACE",FACE,{"disambiguationData":[OSD([sQuery(id+"F8.wireOp",EDGE,"E21"),sQuery(id+"F9.wireOp",EDGE,"E22")])]}),"instanceName":"5"})]});
            var Q1;
            Q1=makeQuery(id+"F15.opBoolean","INTERSECT",EDGE,{"derivedFrom":[makeQuery(id+"F1.opRevolve","SWEPT_FACE",FACE,{"disambiguationData":[OSD([sQuery(id+"F0.wireOp",EDGE,"E16")])]}),makeQuery(id+"F11.opPattern","COPY",FACE,{"derivedFrom":makeQuery(id+"F10.opLoft","SWEPT_FACE",FACE,{"disambiguationData":[OSD([sQuery(id+"F8.wireOp",EDGE,"E21"),sQuery(id+"F9.wireOp",EDGE,"E22")])]}),"instanceName":"6"})]});
            var Q2;
            Q2=makeQuery(id+"F15.opBoolean","INTERSECT",EDGE,{"derivedFrom":[makeQuery(id+"F1.opRevolve","SWEPT_FACE",FACE,{"disambiguationData":[OSD([sQuery(id+"F0.wireOp",EDGE,"E16")])]}),makeQuery(id+"F11.opPattern","COPY",FACE,{"derivedFrom":makeQuery(id+"F10.opLoft","SWEPT_FACE",FACE,{"disambiguationData":[OSD([sQuery(id+"F8.wireOp",EDGE,"E21"),sQuery(id+"F9.wireOp",EDGE,"E22")])]}),"instanceName":"4"})]});
            var Q3;
            Q3=makeQuery(id+"F15.opBoolean","INTERSECT",EDGE,{"derivedFrom":[makeQuery(id+"F1.opRevolve","SWEPT_FACE",FACE,{"disambiguationData":[OSD([sQuery(id+"F0.wireOp",EDGE,"E16")])]}),makeQuery(id+"F11.opPattern","COPY",FACE,{"derivedFrom":makeQuery(id+"F10.opLoft","SWEPT_FACE",FACE,{"disambiguationData":[OSD([sQuery(id+"F8.wireOp",EDGE,"E21"),sQuery(id+"F9.wireOp",EDGE,"E22")])]}),"instanceName":"3"})]});
            var Q4;
            Q4=makeQuery(id+"F15.opBoolean","INTERSECT",EDGE,{"derivedFrom":[makeQuery(id+"F1.opRevolve","SWEPT_FACE",FACE,{"disambiguationData":[OSD([sQuery(id+"F0.wireOp",EDGE,"E16")])]}),makeQuery(id+"F11.opPattern","COPY",FACE,{"derivedFrom":makeQuery(id+"F10.opLoft","SWEPT_FACE",FACE,{"disambiguationData":[OSD([sQuery(id+"F8.wireOp",EDGE,"E21"),sQuery(id+"F9.wireOp",EDGE,"E22")])]}),"instanceName":"2"})]});
            var Q5;
            Q5=makeQuery(id+"F15.opBoolean","INTERSECT",EDGE,{"derivedFrom":[makeQuery(id+"F1.opRevolve","SWEPT_FACE",FACE,{"disambiguationData":[OSD([sQuery(id+"F0.wireOp",EDGE,"E16")])]}),makeQuery(id+"F11.opPattern","COPY",FACE,{"derivedFrom":makeQuery(id+"F10.opLoft","SWEPT_FACE",FACE,{"disambiguationData":[OSD([sQuery(id+"F8.wireOp",EDGE,"E21"),sQuery(id+"F9.wireOp",EDGE,"E22")])]}),"instanceName":"1"})]});
            var Q6;
            Q6=makeQuery(id+"F15.opBoolean","INTERSECT",EDGE,{"derivedFrom":[makeQuery(id+"F1.opRevolve","SWEPT_FACE",FACE,{"disambiguationData":[OSD([sQuery(id+"F0.wireOp",EDGE,"E16")])]}),makeQuery(id+"F10.opLoft","SWEPT_FACE",FACE,{"disambiguationData":[OSD([sQuery(id+"F8.wireOp",EDGE,"E21"),sQuery(id+"F9.wireOp",EDGE,"E22")])]})]});
            var Q7;
            Q7=makeQuery(id+"F15.opBoolean","INTERSECT",EDGE,{"derivedFrom":[makeQuery(id+"F1.opRevolve","SWEPT_FACE",FACE,{"disambiguationData":[OSD([sQuery(id+"F0.wireOp",EDGE,"E16")])]}),makeQuery(id+"F11.opPattern","COPY",FACE,{"derivedFrom":makeQuery(id+"F10.opLoft","SWEPT_FACE",FACE,{"disambiguationData":[OSD([sQuery(id+"F8.wireOp",EDGE,"E21"),sQuery(id+"F9.wireOp",EDGE,"E22")])]}),"instanceName":"11"})]});
            var Q8;
            Q8=makeQuery(id+"F15.opBoolean","INTERSECT",EDGE,{"derivedFrom":[makeQuery(id+"F1.opRevolve","SWEPT_FACE",FACE,{"disambiguationData":[OSD([sQuery(id+"F0.wireOp",EDGE,"E16")])]}),makeQuery(id+"F11.opPattern","COPY",FACE,{"derivedFrom":makeQuery(id+"F10.opLoft","SWEPT_FACE",FACE,{"disambiguationData":[OSD([sQuery(id+"F8.wireOp",EDGE,"E21"),sQuery(id+"F9.wireOp",EDGE,"E22")])]}),"instanceName":"10"})]});
            var Q9;
            Q9=makeQuery(id+"F15.opBoolean","INTERSECT",EDGE,{"derivedFrom":[makeQuery(id+"F1.opRevolve","SWEPT_FACE",FACE,{"disambiguationData":[OSD([sQuery(id+"F0.wireOp",EDGE,"E16")])]}),makeQuery(id+"F11.opPattern","COPY",FACE,{"derivedFrom":makeQuery(id+"F10.opLoft","SWEPT_FACE",FACE,{"disambiguationData":[OSD([sQuery(id+"F8.wireOp",EDGE,"E21"),sQuery(id+"F9.wireOp",EDGE,"E22")])]}),"instanceName":"9"})]});
            var Q10;
            Q10=makeQuery(id+"F15.opBoolean","INTERSECT",EDGE,{"derivedFrom":[makeQuery(id+"F1.opRevolve","SWEPT_FACE",FACE,{"disambiguationData":[OSD([sQuery(id+"F0.wireOp",EDGE,"E16")])]}),makeQuery(id+"F11.opPattern","COPY",FACE,{"derivedFrom":makeQuery(id+"F10.opLoft","SWEPT_FACE",FACE,{"disambiguationData":[OSD([sQuery(id+"F8.wireOp",EDGE,"E21"),sQuery(id+"F9.wireOp",EDGE,"E22")])]}),"instanceName":"8"})]});
            var Q11;
            Q11=makeQuery(id+"F15.opBoolean","INTERSECT",EDGE,{"derivedFrom":[makeQuery(id+"F1.opRevolve","SWEPT_FACE",FACE,{"disambiguationData":[OSD([sQuery(id+"F0.wireOp",EDGE,"E16")])]}),makeQuery(id+"F11.opPattern","COPY",FACE,{"derivedFrom":makeQuery(id+"F10.opLoft","SWEPT_FACE",FACE,{"disambiguationData":[OSD([sQuery(id+"F8.wireOp",EDGE,"E21"),sQuery(id+"F9.wireOp",EDGE,"E22")])]}),"instanceName":"7"})]});
            fillet(context, id + "F16", {"entities" : qUnion([Q0, Q1, Q2, Q3, Q4, Q5, Q6, Q7, Q8, Q9, Q10, Q11]), "radius" : 5.08 * mm, "tangentPropagation" : true, "allowEdgeOverflow" : false});
        }
    });
